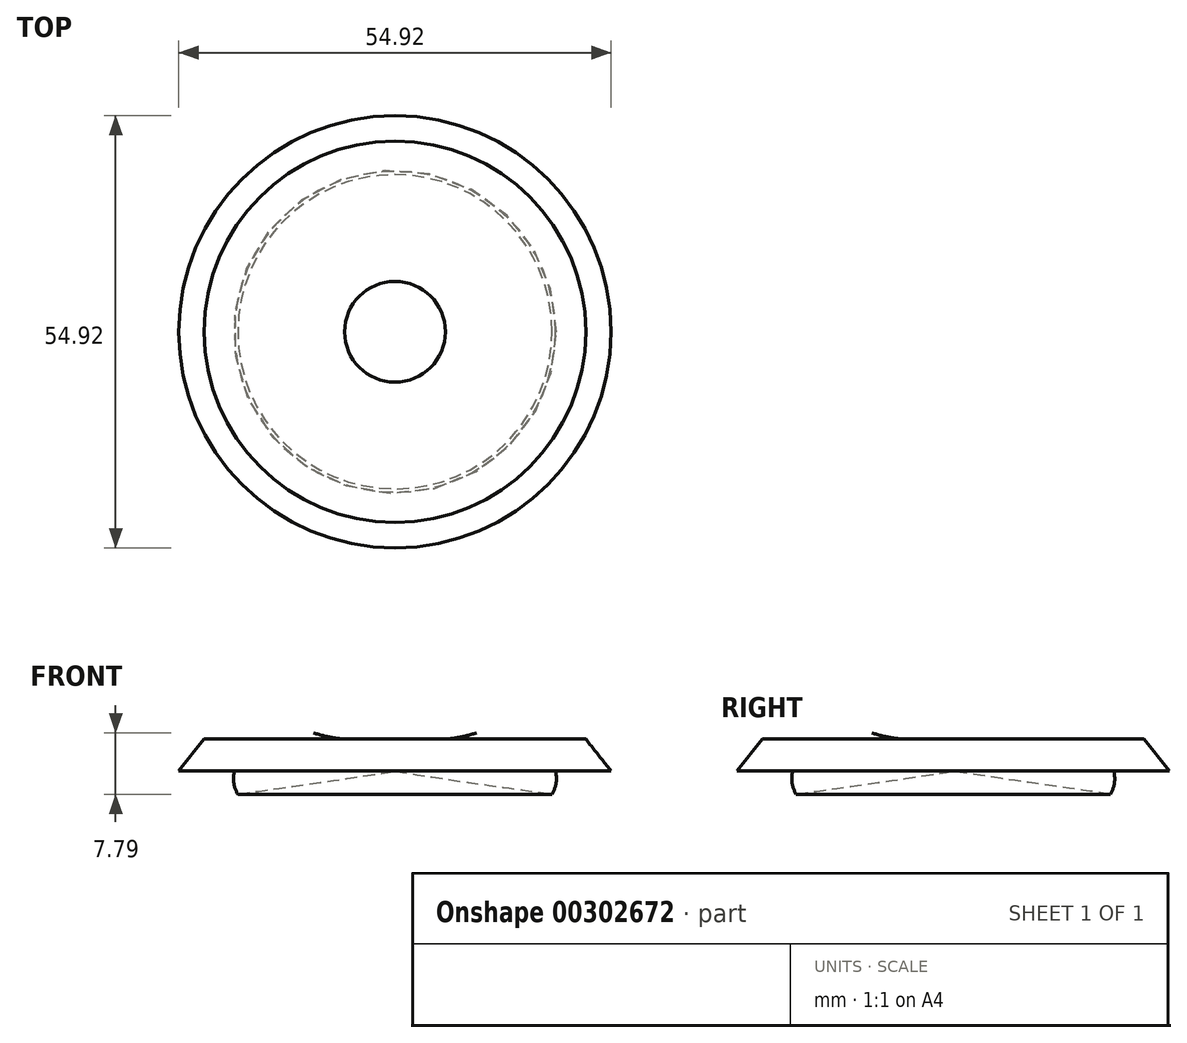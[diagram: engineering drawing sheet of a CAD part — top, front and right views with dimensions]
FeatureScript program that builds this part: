
annotation { "Feature Type Name" : "Feature", "Feature Type Description" : "" }
export const myFeature = defineFeature(function(context is Context, id is Id, definition is map)
    precondition{}
    {
        {
            var Q0;
            Q0=qCreatedBy(makeId("Front.planeOp"),FACE);
            var sketch = newSketch(context, id + "F0", { "sketchPlane" : qUnion([Q0])});
            skArc(sketch, "E0", {"start": v(6.4, -3.74) * mm, "mid": v(21.25, 15.84) * mm, "end": v(0, 28.18) * mm});
            skLineSegment(sketch, "E1", {"start": v(6.4, -3.74) * mm, "end": v(24.24, -3.74) * mm});
            skLineSegment(sketch, "E2", {"start": v(24.24, -3.74) * mm, "end": v(27.46, -7.8) * mm});
            skLineSegment(sketch, "E3", {"start": v(27.46, -7.8) * mm, "end": v(20.39, -7.8) * mm});
            skFitSpline(sketch, "E4", {"points": [v(0, -7.8) * mm, v(28.77, -12.63) * mm, v(28.97, -13.42) * mm, v(10.84, -18.15) * mm, v(27.4, -20.71) * mm, v(18.92, -32.34) * mm, v(31.53, -34.31) * mm, v(35.28, -37.86) * mm, v(35.28, -38.06) * mm], "startDerivative": vector(178.73, -30.02) * mm, "endDerivative": vector(-1.8, -7.67) * mm});
            skLineSegment(sketch, "E5", {"start": v(35.29, -38.01) * mm, "end": v(0, -38.01) * mm});
            skLineSegment(sketch, "E6", {"start": v(0, 28.18) * mm, "end": v(0, -38.01) * mm});
            skPoint(sketch, "E7.orphan", {"position": v(0, -2.96) * mm});
            skPoint(sketch, "E8.orphan", {"position": v(0, -3.74) * mm});
            skArc(sketch, "E9", {"start": v(19.96, -10.75) * mm, "mid": v(20.47, -9.32) * mm, "end": v(20.39, -7.8) * mm});
            skSolve(sketch);
        }
        {
            var Q0;
            Q0=makeQuery(id+"F0.imprint","IMPRINT",FACE,{"disambiguationData":[TD([[makeQuery(id+"F0.imprint","IMPRINT",EDGE,{"derivedFrom":sQuery(id+"F0.wireOp",EDGE,"E0")}),1.0]])]});
            var Q1;
            Q1=sQuery(id+"F0.wireOp",EDGE,"E6");
            revolve(context, id + "F1", {"entities" : qUnion([Q0]), "axis" : qUnion([Q1]), "revolveType" : RevolveType.FULL});
        }
    });
